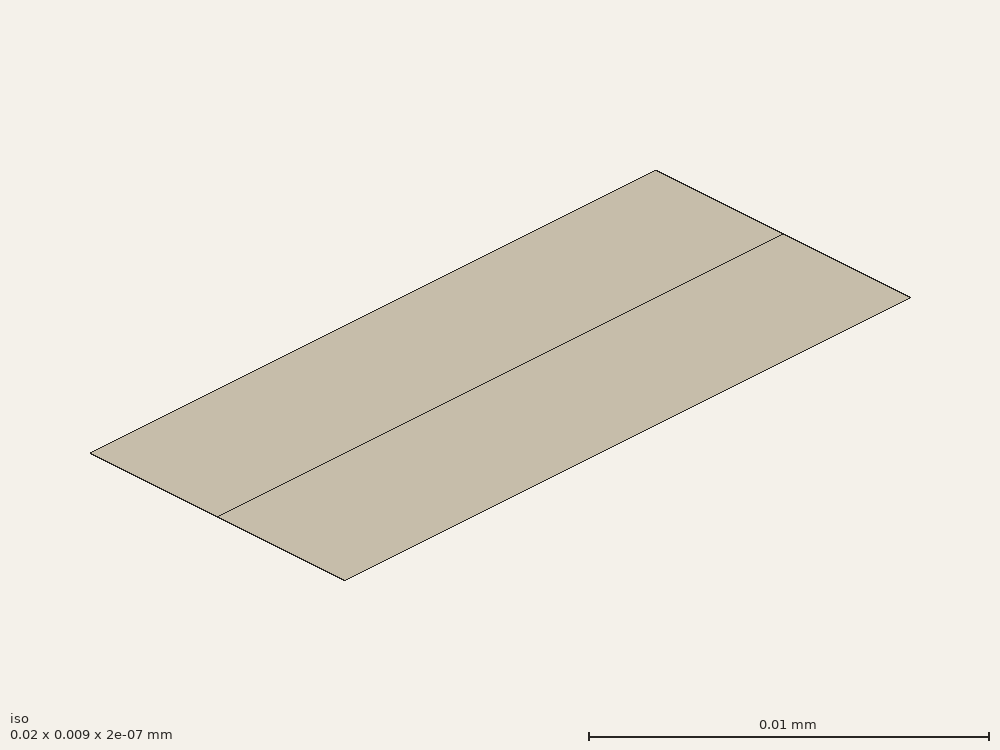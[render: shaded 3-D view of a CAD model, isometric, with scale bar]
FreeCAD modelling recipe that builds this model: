
FCSTD DOCUMENT  (FreeCAD 0.19R)
Label: partially_filled_waveguide
License: All rights reserved
LicenseURL: http://en.wikipedia.org/wiki/All_rights_reserved
objects: Part::Part2DObjectPython×2, Part::FeaturePython×1
note: 3 computed .brp shape members not serialized (recipe doc carries the construction recipe); baked Part::Feature solids carry a one-line shape summary decoded from their .brp

FEATURE [Part::Part2DObjectPython] Rectangle  label="air"  # Draft 2D object (typed FeaturePython)
  Area = 9e-05
  ChamferSize = 0
  Columns = 1
  FilletRadius = 0
  Height = 0.0045
  Length = 0.02
  MakeFace = true
  Placement = pos=(0,0.0045,0) rot=(0,0,1;0rad)
  Rows = 1
FEATURE [Part::Part2DObjectPython] Rectangle001  label="teflon"  # Draft 2D object (typed FeaturePython)
  Area = 9e-05
  ChamferSize = 0
  Columns = 1
  FilletRadius = 0
  Height = 0.0045
  Length = 0.02
  MakeFace = true
  Rows = 1
FEATURE [Part::FeaturePython] BooleanFragments  # WARN: FeaturePython — macro-defined, semantics opaque (R4)
  Mode = 0
  Objects = -> [Rectangle001,Rectangle]
  Tolerance = 0
